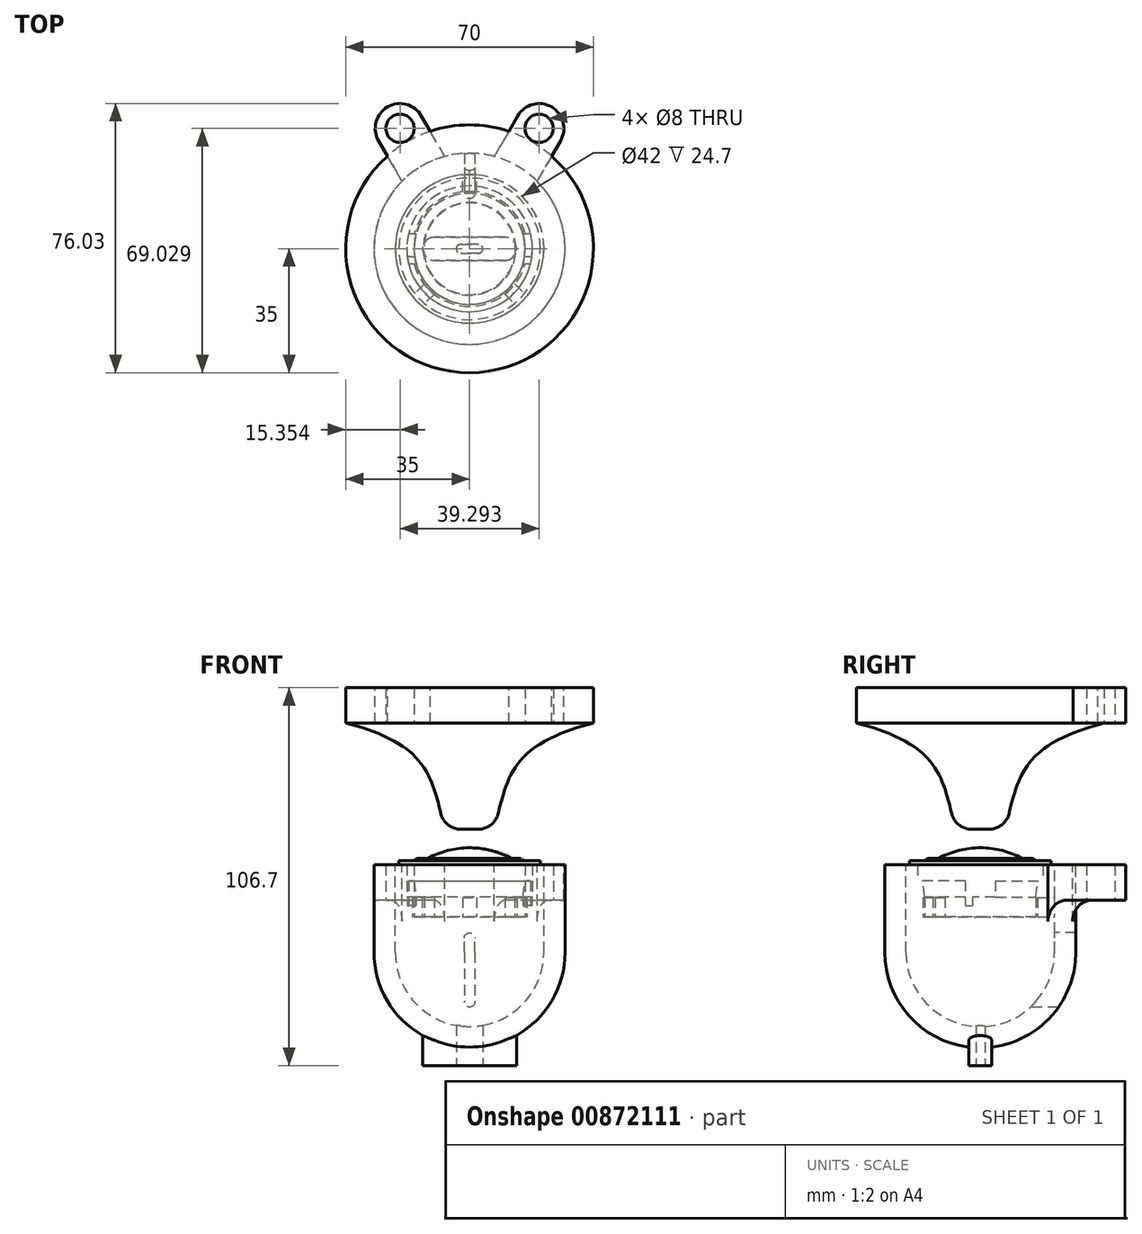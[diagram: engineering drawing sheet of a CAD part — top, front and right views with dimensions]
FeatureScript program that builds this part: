
annotation { "Feature Type Name" : "Feature", "Feature Type Description" : "" }
export const myFeature = defineFeature(function(context is Context, id is Id, definition is map)
    precondition{}
    {
        {
            var Q0;
            Q0=qCreatedBy(makeId("Top.planeOp"),FACE);
            var sketch = newSketch(context, id + "F0", { "sketchPlane" : qUnion([Q0])});
            skCircle(sketch, "E0", {"center": v(0, 0) * mm, "radius": 15.7 * mm});
            skSolve(sketch);
        }
        {
            var Q0;
            Q0 = qSketchRegion(id + "F0", true);
            extrude(context, id + "F1", {"entities" : qUnion([Q0]), "depth" : 5.6 * mm, "offsetDistance" : 25 * mm});
        }
        {
            var Q0;
            Q0=makeQuery(id+"F1.opExtrude","CAP_FACE",FACE,{"disambiguationData":[OSD([sQuery(id+"F0.wireOp",EDGE,"E0")])],"isStart":false});
            cPlane(context, id + "F2", {"entities" : qUnion([Q0]), "cplaneType" : CPlaneType.OFFSET, "offset" : 4.6 * mm, "width" : 150 * mm, "height" : 150 * mm});
        }
        {
            var Q0;
            Q0=makeQuery(id+"F1.opExtrude","CAP_FACE",FACE,{"disambiguationData":[OSD([sQuery(id+"F0.wireOp",EDGE,"E0")])],"isStart":false});
            var sketch = newSketch(context, id + "F3", { "sketchPlane" : qUnion([Q0])});
            skCircle(sketch, "E1.0", {"center": v(0, 0) * mm, "radius": 15.7 * mm});
            skSolve(sketch);
        }
        {
            var Q0;
            Q0=qCreatedBy(id+"F2.planeOp",FACE);
            var sketch = newSketch(context, id + "F4", { "sketchPlane" : qUnion([Q0])});
            skCircle(sketch, "E2", {"center": v(0, 0) * mm, "radius": 16.25 * mm});
            skSolve(sketch);
        }
        {
            var Q1;
            Q1=makeQuery(id+"F3.imprint","IMPRINT",FACE,{"disambiguationData":[TD([[makeQuery(id+"F3.imprint","IMPRINT",EDGE,{"derivedFrom":sQuery(id+"F3.wireOp",EDGE,"E1.0")}),1.0]])]});
            var Q2;
            Q2=makeQuery(id+"F4.imprint","IMPRINT",FACE,{"disambiguationData":[TD([[makeQuery(id+"F4.imprint","IMPRINT",EDGE,{"derivedFrom":sQuery(id+"F4.wireOp",EDGE,"E2")}),1.0]])]});
            loft(context, id + "F5", {"operationType" : NewBodyOperationType.ADD, "sheetProfilesArray" : [{ "sheetProfileEntities" : qUnion([Q1]) }, { "sheetProfileEntities" : qUnion([Q2]) }]});
        }
        {
            var Q0;
            Q0=makeQuery(id+"F5.opLoft","CAP_FACE",FACE,{"disambiguationData":[OSD([makeQuery(id+"F4.imprint","IMPRINT",FACE,{"disambiguationData":[TD([[makeQuery(id+"F4.imprint","IMPRINT",EDGE,{"derivedFrom":sQuery(id+"F4.wireOp",EDGE,"E2")}),1.0]])]})])],"isStart":true});
            var sketch = newSketch(context, id + "F6", { "sketchPlane" : qUnion([Q0])});
            skCircle(sketch, "E3", {"center": v(0, 0) * mm, "radius": 17.75 * mm});
            skSolve(sketch);
        }
        {
            var Q0;
            Q0 = qSketchRegion(id + "F6", true);
            extrude(context, id + "F7", {"entities" : qUnion([Q0]), "operationType" : NewBodyOperationType.ADD, "depth" : 4.5 * mm, "offsetDistance" : 25 * mm});
        }
        {
            var Q0;
            Q0=makeQuery(id+"F7.opExtrude","CAP_FACE",FACE,{"disambiguationData":[OSD([sQuery(id+"F6.wireOp",EDGE,"E3")])],"isStart":false});
            var sketch = newSketch(context, id + "F8", { "sketchPlane" : qUnion([Q0])});
            skCircle(sketch, "E4", {"center": v(0, 0) * mm, "radius": 20 * mm});
            skSolve(sketch);
        }
        {
            var Q0;
            Q0 = qSketchRegion(id + "F8", true);
            extrude(context, id + "F9", {"entities" : qUnion([Q0]), "operationType" : NewBodyOperationType.ADD, "depth" : 1.2 * mm, "offsetDistance" : 25 * mm});
        }
        {
            var Q0;
            Q0=qCreatedBy(makeId("Front.planeOp"),FACE);
            var sketch = newSketch(context, id + "F10", { "sketchPlane" : qUnion([Q0])});
            skCircle(sketch, "E5", {"center": v(-14.38, 14.9) * mm, "radius": 1.62 * mm});
            skLineSegment(sketch, "E6", {"start": v(-12.75, 17.4) * mm, "end": v(-12.75, 14.93) * mm, "construction": true});
            skLineSegment(sketch, "E7", {"start": v(-16, 17.73) * mm, "end": v(-16, 14.12) * mm, "construction": true});
            skSolve(sketch);
        }
        {
            var Q0;
            Q0 = qSketchRegion(id + "F10", true);
            var Q1;
            Q1=makeQuery(id+"F1.opExtrude","SWEPT_FACE",FACE,{"disambiguationData":[OSD([sQuery(id+"F0.wireOp",EDGE,"E0")])]});
            revolve(context, id + "F11", {"operationType" : NewBodyOperationType.ADD, "surfaceOperationType" : NewSurfaceOperationType.NEW, "entities" : qUnion([Q0]), "axis" : qUnion([Q1]), "revolveType" : RevolveType.FULL});
        }
        {
            var Q0;
            Q0=qCreatedBy(makeId("Front.planeOp"),FACE);
            var sketch = newSketch(context, id + "F12", { "sketchPlane" : qUnion([Q0])});
            skArc(sketch, "E8", {"start": v(0, 19.5) * mm, "mid": v(-8.14, 18.14) * mm, "end": v(-15.4, 14.2) * mm});
            skLineSegment(sketch, "E9", {"start": v(-9, 19.5) * mm, "end": v(9, 19.5) * mm, "construction": true});
            skLineSegment(sketch, "E10", {"start": v(-15.4, 14.2) * mm, "end": v(0, 14.2) * mm});
            skLineSegment(sketch, "E11", {"start": v(0, 21.06) * mm, "end": v(0, 12) * mm});
            skSolve(sketch);
        }
        {
            var Q0;
            Q0 = qSketchRegion(id + "F12", true);
            var Q1;
            Q1=sQuery(id+"F12.wireOp",EDGE,"E11");
            revolve(context, id + "F13", {"operationType" : NewBodyOperationType.ADD, "surfaceOperationType" : NewSurfaceOperationType.NEW, "entities" : qUnion([Q0]), "axis" : qUnion([Q1]), "revolveType" : RevolveType.FULL});
        }
        {
            var Q0;
            Q0=qCreatedBy(makeId("Right.planeOp"),FACE);
            var sketch = newSketch(context, id + "F14", { "sketchPlane" : qUnion([Q0])});
            skLineSegment(sketch, "E12.bottom", {"start": v(-4.25, 10.2) * mm, "end": v(4.25, 10.2) * mm});
            skLineSegment(sketch, "E12.top", {"start": v(-4.25, 5.6) * mm, "end": v(4.25, 5.6) * mm});
            skLineSegment(sketch, "E12.left", {"start": v(-4.25, 10.2) * mm, "end": v(-4.25, 5.6) * mm});
            skLineSegment(sketch, "E12.right", {"start": v(4.25, 10.2) * mm, "end": v(4.25, 5.6) * mm});
            skPoint(sketch, "E13", {"position": v(0, 5.6) * mm});
            skLineSegment(sketch, "E14.bottom", {"start": v(-4.25, 5.6) * mm, "end": v(-2.25, 5.6) * mm});
            skLineSegment(sketch, "E14.top", {"start": v(-4.25, 3.1) * mm, "end": v(-2.25, 3.1) * mm});
            skLineSegment(sketch, "E14.left", {"start": v(-4.25, 5.6) * mm, "end": v(-4.25, 3.1) * mm});
            skLineSegment(sketch, "E14.right", {"start": v(-2.25, 5.6) * mm, "end": v(-2.25, 3.1) * mm});
            skSolve(sketch);
        }
        {
            var Q0;
            Q0 = qSketchRegion(id + "F14", true);
            var Q1;
            Q1=makeQuery(id+"F7.opExtrude","SWEPT_FACE",FACE,{"disambiguationData":[OSD([sQuery(id+"F6.wireOp",EDGE,"E3")])]});
            var Q2;
            Q2=makeQuery(id+"F7.opExtrude","SWEPT_FACE",FACE,{"disambiguationData":[OSD([sQuery(id+"F6.wireOp",EDGE,"E3")])]});
            extrude(context, id + "F15", {"entities" : qUnion([Q0]), "operationType" : NewBodyOperationType.ADD, "endBound" : BoundingType.UP_TO_SURFACE, "depth" : 25 * mm, "endBoundEntityFace" : qUnion([Q1]), "offsetDistance" : 25 * mm, "hasSecondDirection" : true, "secondDirectionBound" : BoundingType.UP_TO_SURFACE, "secondDirectionOppositeDirection" : true, "secondDirectionDepth" : 25 * mm, "secondDirectionBoundEntityFace" : qUnion([Q2])});
        }
        {
            var Q0;
            Q0=qCreatedBy(makeId("Front.planeOp"),FACE);
            var sketch = newSketch(context, id + "F16", { "sketchPlane" : qUnion([Q0])});
            skLineSegment(sketch, "E15", {"start": v(-21, 14.7) * mm, "end": v(-21, -10) * mm});
            skArc(sketch, "E16", {"start": v(-21, -10) * mm, "mid": v(-14.85, -24.85) * mm, "end": v(0, -31) * mm});
            skLineSegment(sketch, "E17", {"start": v(0, 25.8) * mm, "end": v(0, -46.07) * mm, "construction": true});
            skArc(sketch, "E18.0", {"start": v(-27, -10) * mm, "mid": v(-19.1, -29.1) * mm, "end": v(0, -37) * mm});
            skLineSegment(sketch, "E18.1", {"start": v(-27, 14.7) * mm, "end": v(-27, -10) * mm});
            skLineSegment(sketch, "E19", {"start": v(-27, 14.7) * mm, "end": v(-21, 14.7) * mm});
            skLineSegment(sketch, "E20", {"start": v(0, -31) * mm, "end": v(0, -37) * mm});
            skSolve(sketch);
        }
        {
            var Q0;
            Q0 = qSketchRegion(id + "F16", true);
            var Q1;
            Q1=sQuery(id+"F16.wireOp",EDGE,"E17");
            revolve(context, id + "F17", {"surfaceOperationType" : NewSurfaceOperationType.NEW, "entities" : qUnion([Q0]), "axis" : qUnion([Q1]), "revolveType" : RevolveType.FULL});
        }
        {
            var Q0;
            Q0=makeQuery(id+"F1.opExtrude","CAP_FACE",FACE,{"disambiguationData":[OSD([sQuery(id+"F0.wireOp",EDGE,"E0")])],"isStart":true});
            var sketch = newSketch(context, id + "F18", { "sketchPlane" : qUnion([Q0])});
            skLineSegment(sketch, "E21", {"start": v(0, 0) * mm, "end": v(0, -21) * mm, "construction": true});
            skLineSegment(sketch, "E22", {"start": v(0, 0) * mm, "end": v(14.85, 14.85) * mm, "construction": true});
            skLineSegment(sketch, "E23", {"start": v(0, 0) * mm, "end": v(-14.85, 14.85) * mm, "construction": true});
            skArc(sketch, "E24.0", {"start": v(-9.95, 12.78) * mm, "mid": v(-11.46, 11.46) * mm, "end": v(-12.78, 9.95) * mm});
            skArc(sketch, "E25", {"start": v(-13.37, 16.2) * mm, "mid": v(-14.85, 14.85) * mm, "end": v(-16.2, 13.37) * mm});
            skLineSegment(sketch, "E26.0", {"start": v(-9.95, 12.78) * mm, "end": v(-13.37, 16.2) * mm});
            skLineSegment(sketch, "E26.1", {"start": v(9.95, 12.78) * mm, "end": v(13.37, 16.2) * mm});
            skLineSegment(sketch, "E27.0", {"start": v(-12.78, 9.95) * mm, "end": v(-16.2, 13.37) * mm});
            skLineSegment(sketch, "E27.1", {"start": v(12.78, 9.95) * mm, "end": v(16.2, 13.37) * mm});
            skLineSegment(sketch, "E28.0", {"start": v(-2, -16.08) * mm, "end": v(-2, -20.9) * mm});
            skLineSegment(sketch, "E29.0", {"start": v(2, -16.08) * mm, "end": v(2, -20.9) * mm});
            skArc(sketch, "E30.trimOffspring", {"start": v(-2, -20.9) * mm, "mid": v(0, -21) * mm, "end": v(2, -20.9) * mm});
            skArc(sketch, "E31.trimOffspring", {"start": v(-2, -16.08) * mm, "mid": v(0, -16.2) * mm, "end": v(2, -16.08) * mm});
            skArc(sketch, "E32.trimOffspring", {"start": v(12.78, 9.95) * mm, "mid": v(11.46, 11.46) * mm, "end": v(9.95, 12.78) * mm});
            skArc(sketch, "E33.trimOffspring", {"start": v(16.2, 13.37) * mm, "mid": v(14.85, 14.85) * mm, "end": v(13.37, 16.2) * mm});
            skSolve(sketch);
        }
        {
            var Q0;
            Q0 = qSketchRegion(id + "F18", true);
            var Q1;
            {var subQ1=sQuery(id+"F14.wireOp",EDGE,"E14.left");var subQ4=sQuery(id+"F14.wireOp",EDGE,"E12.left");var subQ7=sQuery(id+"F6.wireOp",EDGE,"E3");Q1=makeQuery(id+"F15.boolean.opBoolean","SPLIT",FACE,{"disambiguationData":[TD([makeQuery(id+"F15.opExtrude","SWEPT_FACE",FACE,{"disambiguationData":[OSD([subQ4,subQ1])]})])],"derivedFrom":makeQuery(id+"F7.opExtrude","CAP_FACE",FACE,{"disambiguationData":[OSD([subQ7])],"isStart":true})});}
            extrude(context, id + "F19", {"entities" : qUnion([Q0]), "operationType" : NewBodyOperationType.ADD, "oppositeDirection" : true, "depth" : 5.5 * mm, "endBoundEntityFace" : qUnion([Q1]), "offsetDistance" : 25 * mm});
        }
        {
            var Q0;
            Q0=qCreatedBy(makeId("Front.planeOp"),FACE);
            var sketch = newSketch(context, id + "F20", { "sketchPlane" : qUnion([Q0])});
            skLineSegment(sketch, "E34", {"start": v(0, -6) * mm, "end": v(0, -24) * mm});
            skArc(sketch, "E35.0.startCap", {"start": v(-1.5, -6) * mm, "mid": v(0, -4.5) * mm, "end": v(1.5, -6) * mm});
            skArc(sketch, "E35.0.endCap", {"start": v(1.5, -24) * mm, "mid": v(0, -25.5) * mm, "end": v(-1.5, -24) * mm});
            skLineSegment(sketch, "E35.0.left", {"start": v(1.5, -6) * mm, "end": v(1.5, -24) * mm});
            skLineSegment(sketch, "E35.0.right", {"start": v(-1.5, -6) * mm, "end": v(-1.5, -24) * mm});
            skSolve(sketch);
        }
        {
            var Q0;
            Q0 = qSketchRegion(id + "F20", true);
            extrude(context, id + "F21", {"entities" : qUnion([Q0]), "operationType" : NewBodyOperationType.REMOVE, "endBound" : BoundingType.THROUGH_ALL, "oppositeDirection" : true, "depth" : 25 * mm, "offsetDistance" : 25 * mm});
        }
        {
            var Q0;
            Q0=sQuery(id+"F16.wireOp",EDGE,"E17");
            var Q1;
            Q1=sQuery(id+"F16.wireOp",VERTEX,"E18.0.end");
            cPlane(context, id + "F22", {"entities" : qUnion([Q0, Q1]), "cplaneType" : CPlaneType.LINE_POINT, "offset" : 25 * mm, "width" : 150 * mm, "height" : 150 * mm});
        }
        {
            var Q0;
            Q0=qCreatedBy(id+"F22.planeOp",FACE);
            var sketch = newSketch(context, id + "F23", { "sketchPlane" : qUnion([Q0])});
            skLineSegment(sketch, "E36", {"start": v(-10, 0) * mm, "end": v(10, 0) * mm});
            skArc(sketch, "E37.0.startCap", {"start": v(-10, -3.25) * mm, "mid": v(-13.25, 0) * mm, "end": v(-10, 3.25) * mm});
            skArc(sketch, "E37.0.endCap", {"start": v(10, 3.25) * mm, "mid": v(13.25, 0) * mm, "end": v(10, -3.25) * mm});
            skLineSegment(sketch, "E37.0.left", {"start": v(-10, 3.25) * mm, "end": v(10, 3.25) * mm});
            skLineSegment(sketch, "E37.0.right", {"start": v(-10, -3.25) * mm, "end": v(10, -3.25) * mm});
            skArc(sketch, "E38.0.startCap", {"start": v(-10, -3.25) * mm, "mid": v(-13.25, 0) * mm, "end": v(-10, 3.25) * mm, "construction": true});
            skArc(sketch, "E38.0.endCap", {"start": v(10, 3.25) * mm, "mid": v(13.25, 0) * mm, "end": v(10, -3.25) * mm, "construction": true});
            skLineSegment(sketch, "E38.0.left", {"start": v(-10, 3.25) * mm, "end": v(10, 3.25) * mm, "construction": true});
            skLineSegment(sketch, "E38.0.right", {"start": v(-10, -3.25) * mm, "end": v(10, -3.25) * mm, "construction": true});
            skSolve(sketch);
        }
        {
            var Q0;
            Q0 = qSketchRegion(id + "F23", true);
            extrude(context, id + "F24", {"entities" : qUnion([Q0]), "operationType" : NewBodyOperationType.ADD, "endBound" : BoundingType.UP_TO_NEXT, "oppositeDirection" : true, "depth" : 25 * mm, "offsetDistance" : 25 * mm, "hasSecondDirection" : true, "secondDirectionOppositeDirection" : false, "secondDirectionDepth" : 5 * mm});
        }
        {
            var Q0;
            Q0=makeQuery(id+"F17.opRevolve","SWEPT_FACE",FACE,{"disambiguationData":[OSD([sQuery(id+"F16.wireOp",EDGE,"E19")])]});
            cPlane(context, id + "F25", {"entities" : qUnion([Q0]), "cplaneType" : CPlaneType.OFFSET, "offset" : 10 * mm, "width" : 150 * mm, "height" : 150 * mm});
        }
        {
            var Q0;
            Q0=qCreatedBy(id+"F25.planeOp",FACE);
            var sketch = newSketch(context, id + "F26", { "sketchPlane" : qUnion([Q0])});
            skCircle(sketch, "E39", {"center": v(0, 0) * mm, "radius": 7.5 * mm});
            skPoint(sketch, "E40", {"position": v(-7.5, 0) * mm});
            skSolve(sketch);
        }
        {
            var Q0;
            Q0=qCreatedBy(id+"F25.planeOp",FACE);
            cPlane(context, id + "F27", {"entities" : qUnion([Q0]), "cplaneType" : CPlaneType.OFFSET, "offset" : 30 * mm, "width" : 150 * mm, "height" : 150 * mm});
        }
        {
            var Q0;
            Q0=qCreatedBy(id+"F27.planeOp",FACE);
            var sketch = newSketch(context, id + "F28", { "sketchPlane" : qUnion([Q0])});
            skCircle(sketch, "E41", {"center": v(0, 0) * mm, "radius": 35 * mm});
            skPoint(sketch, "E42", {"position": v(-35, 0) * mm});
            skSolve(sketch);
        }
        {
            var Q0;
            Q0=qCreatedBy(makeId("Front.planeOp"),FACE);
            var sketch = newSketch(context, id + "F29", { "sketchPlane" : qUnion([Q0])});
            skPoint(sketch, "E43", {"position": v(-12.77, 42) * mm});
            skPoint(sketch, "E44", {"position": v(-9, 32.7) * mm});
            skFitSpline(sketch, "E45", {"points": [v(-7.5, 24.7) * mm, v(-9, 32.7) * mm, v(-12.77, 42) * mm, v(-35, 54.7) * mm], "startDerivative": vector(-5.93, 52) * mm, "endDerivative": vector(-83.34, 20.66) * mm});
            skLineSegment(sketch, "E46", {"start": v(0, 54.7) * mm, "end": v(0, 24.7) * mm});
            skLineSegment(sketch, "E47", {"start": v(-35, 54.7) * mm, "end": v(0, 54.7) * mm});
            skLineSegment(sketch, "E48", {"start": v(0, 24.7) * mm, "end": v(-7.5, 24.7) * mm});
            skSolve(sketch);
        }
        {
            var Q0;
            Q0=makeQuery(id+"F29.imprint","IMPRINT",FACE,{"disambiguationData":[TD([[makeQuery(id+"F29.imprint","IMPRINT",EDGE,{"derivedFrom":sQuery(id+"F29.wireOp",EDGE,"E45")}),-1.0]])]});
            var Q1;
            Q1=sQuery(id+"F29.wireOp",EDGE,"E46");
            revolve(context, id + "F30", {"surfaceOperationType" : NewSurfaceOperationType.NEW, "entities" : qUnion([Q0]), "axis" : qUnion([Q1]), "revolveType" : RevolveType.FULL});
        }
        {
            var Q0;
            Q0=makeQuery(id+"F30.opRevolve","SWEPT_FACE",FACE,{"disambiguationData":[OSD([sQuery(id+"F29.wireOp",EDGE,"E47")])]});
            var sketch = newSketch(context, id + "F31", { "sketchPlane" : qUnion([Q0])});
            skCircle(sketch, "E49.0", {"center": v(0, 0) * mm, "radius": 35 * mm});
            skSolve(sketch);
        }
        {
            var Q0;
            Q0 = qSketchRegion(id + "F31", true);
            extrude(context, id + "F32", {"entities" : qUnion([Q0]), "operationType" : NewBodyOperationType.ADD, "depth" : 10 * mm, "offsetDistance" : 25 * mm});
        }
        {
            var Q0;
            Q0=makeQuery(id+"F24.opExtrude","CAP_FACE",FACE,{"disambiguationData":[OSD([sQuery(id+"F23.wireOp",EDGE,"E37.0.startCap"),sQuery(id+"F23.wireOp",EDGE,"E37.0.endCap"),sQuery(id+"F23.wireOp",EDGE,"E37.0.left"),sQuery(id+"F23.wireOp",EDGE,"E37.0.right")])],"isStart":true});
            var sketch = newSketch(context, id + "F33", { "sketchPlane" : qUnion([Q0])});
            skLineSegment(sketch, "E50", {"start": v(-2.5, 0) * mm, "end": v(2.5, 0) * mm});
            skArc(sketch, "E51.0.startCap", {"start": v(-2.5, -1.25) * mm, "mid": v(-3.75, 0) * mm, "end": v(-2.5, 1.25) * mm});
            skArc(sketch, "E51.0.endCap", {"start": v(2.5, 1.25) * mm, "mid": v(3.75, 0) * mm, "end": v(2.5, -1.25) * mm});
            skLineSegment(sketch, "E51.0.left", {"start": v(-2.5, 1.25) * mm, "end": v(2.5, 1.25) * mm});
            skLineSegment(sketch, "E51.0.right", {"start": v(-2.5, -1.25) * mm, "end": v(2.5, -1.25) * mm});
            skSolve(sketch);
        }
        {
            var Q0;
            Q0 = qSketchRegion(id + "F33", true);
            extrude(context, id + "F34", {"entities" : qUnion([Q0]), "operationType" : NewBodyOperationType.REMOVE, "endBound" : BoundingType.UP_TO_NEXT, "oppositeDirection" : true, "depth" : 25 * mm, "offsetDistance" : 25 * mm});
        }
        {
            var Q0;
            Q0=makeQuery(id+"F17.opRevolve","SWEPT_FACE",FACE,{"disambiguationData":[OSD([sQuery(id+"F16.wireOp",EDGE,"E19")])]});
            var sketch = newSketch(context, id + "F35", { "sketchPlane" : qUnion([Q0])});
            skLineSegment(sketch, "E52.bottom", {"start": v(-5, -26.53) * mm, "end": v(5, -26.53) * mm});
            skLineSegment(sketch, "E52.top", {"start": v(-5, -33.53) * mm, "end": v(5, -33.53) * mm, "construction": true});
            skLineSegment(sketch, "E52.left", {"start": v(-5, -26.53) * mm, "end": v(-5, -33.53) * mm});
            skLineSegment(sketch, "E52.right", {"start": v(5, -26.53) * mm, "end": v(5, -33.53) * mm});
            skLineSegment(sketch, "E53", {"start": v(0, -33.53) * mm, "end": v(0, 0) * mm, "construction": true});
            skArc(sketch, "E54", {"start": v(-5, -33.53) * mm, "mid": v(0, -38.53) * mm, "end": v(5, -33.53) * mm});
            skSolve(sketch);
        }
        {
            var Q0;
            Q0=makeQuery(id+"F32.opExtrude","CAP_FACE",FACE,{"disambiguationData":[OSD([sQuery(id+"F31.wireOp",EDGE,"E49.0")])],"isStart":false});
            var sketch = newSketch(context, id + "F36", { "sketchPlane" : qUnion([Q0])});
            skLineSegment(sketch, "E55.bottom", {"start": v(-5, -34.64) * mm, "end": v(5, -34.64) * mm});
            skLineSegment(sketch, "E55.top", {"start": v(-5, -39.64) * mm, "end": v(5, -39.64) * mm, "construction": true});
            skLineSegment(sketch, "E55.left", {"start": v(-5, -34.64) * mm, "end": v(-5, -39.64) * mm});
            skLineSegment(sketch, "E55.right", {"start": v(5, -34.64) * mm, "end": v(5, -39.64) * mm});
            skArc(sketch, "E56", {"start": v(-5, -39.64) * mm, "mid": v(0, -44.64) * mm, "end": v(5, -39.64) * mm});
            skLineSegment(sketch, "E57", {"start": v(0, 0) * mm, "end": v(-23.15, 40.1) * mm, "construction": true});
            skLineSegment(sketch, "E58", {"start": v(23.15, 40.1) * mm, "end": v(0, 0) * mm, "construction": true});
            skLineSegment(sketch, "E59", {"start": v(0, 0) * mm, "end": v(0, 42.3) * mm, "construction": true});
            skLineSegment(sketch, "E60.0", {"start": v(-11.08, 33.2) * mm, "end": v(-13.58, 37.53) * mm});
            skLineSegment(sketch, "E61.0", {"start": v(-23.2, 26.2) * mm, "end": v(-25.7, 30.53) * mm});
            skLineSegment(sketch, "E61.1", {"start": v(25.7, 30.53) * mm, "end": v(23.2, 26.2) * mm});
            skLineSegment(sketch, "E62", {"start": v(-23.2, 26.2) * mm, "end": v(-11.08, 33.2) * mm});
            skLineSegment(sketch, "E63", {"start": v(11.08, 33.2) * mm, "end": v(23.2, 26.2) * mm});
            skArc(sketch, "E64", {"start": v(-13.58, 37.53) * mm, "mid": v(-23.15, 40.1) * mm, "end": v(-25.7, 30.53) * mm});
            skArc(sketch, "E65", {"start": v(25.7, 30.53) * mm, "mid": v(23.15, 40.1) * mm, "end": v(13.58, 37.53) * mm});
            skPoint(sketch, "E66.orphan", {"position": v(-27.38, 47.43) * mm});
            skLineSegment(sketch, "E67.trimOffspring", {"start": v(13.58, 37.53) * mm, "end": v(11.08, 33.2) * mm});
            skPoint(sketch, "E68.end.orphan", {"position": v(27.38, 47.43) * mm});
            skLineSegment(sketch, "E69", {"start": v(13.58, 37.53) * mm, "end": v(25.7, 30.53) * mm, "construction": true});
            skSolve(sketch);
        }
        {
            var Q0;
            {var subQ0=sQuery(id+"F36.wireOp",EDGE,"E60.0");Q0=makeQuery(id+"F36.imprint","IMPRINT",FACE,{"disambiguationData":[TD([[makeQuery(id+"F36.imprint","IMPRINT",EDGE,{"derivedFrom":subQ0}),1.0]])]});}
            var Q1;
            {var subQ0=sQuery(id+"F36.wireOp",EDGE,"E61.1");Q1=makeQuery(id+"F36.imprint","IMPRINT",FACE,{"disambiguationData":[TD([[makeQuery(id+"F36.imprint","IMPRINT",EDGE,{"derivedFrom":subQ0}),-1.0]])]});}
            var Q2;
            Q2=makeQuery(id+"F30.opRevolve","SWEPT_FACE",FACE,{"disambiguationData":[OSD([sQuery(id+"F29.wireOp",EDGE,"E45")])]});
            extrude(context, id + "F37", {"entities" : qUnion([Q0, Q1]), "operationType" : NewBodyOperationType.ADD, "oppositeDirection" : true, "depth" : 10 * mm, "endBoundEntityFace" : qUnion([Q2]), "offsetDistance" : 25 * mm});
        }
        {
            var Q0;
            Q0=makeQuery(id+"F17.opRevolve","SWEPT_FACE",FACE,{"disambiguationData":[OSD([sQuery(id+"F16.wireOp",EDGE,"E19")])]});
            var sketch = newSketch(context, id + "F38", { "sketchPlane" : qUnion([Q0])});
            skLineSegment(sketch, "E70.0", {"start": v(25.7, 30.53) * mm, "end": v(23.2, 26.2) * mm});
            skArc(sketch, "E70.1", {"start": v(25.7, 30.53) * mm, "mid": v(23.15, 40.1) * mm, "end": v(13.58, 37.53) * mm});
            skLineSegment(sketch, "E70.2", {"start": v(13.58, 37.53) * mm, "end": v(11.08, 33.2) * mm});
            skLineSegment(sketch, "E70.3", {"start": v(11.08, 33.2) * mm, "end": v(23.2, 26.2) * mm});
            skLineSegment(sketch, "E71.0", {"start": v(-23.2, 26.2) * mm, "end": v(-25.7, 30.53) * mm});
            skLineSegment(sketch, "E71.1", {"start": v(-11.08, 33.2) * mm, "end": v(-13.58, 37.53) * mm});
            skArc(sketch, "E71.2", {"start": v(-13.58, 37.53) * mm, "mid": v(-23.15, 40.1) * mm, "end": v(-25.7, 30.53) * mm});
            skLineSegment(sketch, "E71.3", {"start": v(-23.2, 26.2) * mm, "end": v(-11.08, 33.2) * mm});
            skLineSegment(sketch, "E72", {"start": v(-23.2, 26.2) * mm, "end": v(-19.1, 19.08) * mm});
            skLineSegment(sketch, "E73", {"start": v(-19.1, 19.08) * mm, "end": v(-6.98, 26.08) * mm});
            skLineSegment(sketch, "E74", {"start": v(-6.98, 26.08) * mm, "end": v(-11.08, 33.2) * mm});
            skLineSegment(sketch, "E75", {"start": v(23.2, 26.2) * mm, "end": v(19.1, 19.08) * mm});
            skLineSegment(sketch, "E76", {"start": v(19.1, 19.08) * mm, "end": v(6.98, 26.08) * mm});
            skLineSegment(sketch, "E77", {"start": v(6.98, 26.08) * mm, "end": v(11.08, 33.2) * mm});
            skSolve(sketch);
        }
        {
            var Q0;
            Q0 = qSketchRegion(id + "F38", true);
            extrude(context, id + "F39", {"entities" : qUnion([Q0]), "operationType" : NewBodyOperationType.ADD, "oppositeDirection" : true, "depth" : 10 * mm, "offsetDistance" : 25 * mm});
        }
        {
            var Q0;
            Q0=makeQuery(id+"F37.opExtrude","SWEPT_EDGE",EDGE,{"disambiguationData":[OSD([sQuery(id+"F31.wireOp",EDGE,"E49.0"),sQuery(id+"F36.wireOp",EDGE,"E55.bottom"),sQuery(id+"F36.wireOp",EDGE,"E55.left")])]});
            var Q1;
            Q1=makeQuery(id+"F37.opExtrude","SWEPT_EDGE",EDGE,{"disambiguationData":[OSD([sQuery(id+"F31.wireOp",EDGE,"E49.0"),sQuery(id+"F36.wireOp",EDGE,"E55.bottom"),sQuery(id+"F36.wireOp",EDGE,"E55.right")])]});
            var Q2;
            Q2=makeQuery(id+"F37.opExtrude","SWEPT_EDGE",EDGE,{"disambiguationData":[OSD([sQuery(id+"F31.wireOp",EDGE,"E49.0"),sQuery(id+"F36.wireOp",EDGE,"E61.0"),sQuery(id+"F36.wireOp",EDGE,"E62")])]});
            var Q3;
            Q3=makeQuery(id+"F37.opExtrude","SWEPT_EDGE",EDGE,{"disambiguationData":[OSD([sQuery(id+"F31.wireOp",EDGE,"E49.0"),sQuery(id+"F36.wireOp",EDGE,"E60.0"),sQuery(id+"F36.wireOp",EDGE,"E62")])]});
            var Q4;
            Q4=makeQuery(id+"F37.opExtrude","SWEPT_EDGE",EDGE,{"disambiguationData":[OSD([sQuery(id+"F31.wireOp",EDGE,"E49.0"),sQuery(id+"F36.wireOp",EDGE,"E61.1"),sQuery(id+"F36.wireOp",EDGE,"E63")])]});
            var Q5;
            Q5=makeQuery(id+"F37.opExtrude","SWEPT_EDGE",EDGE,{"disambiguationData":[OSD([sQuery(id+"F31.wireOp",EDGE,"E49.0"),sQuery(id+"F36.wireOp",EDGE,"E63"),sQuery(id+"F36.wireOp",EDGE,"E67.trimOffspring")])]});
            var Q6;
            Q6=makeQuery(id+"F39.opExtrude","SWEPT_EDGE",EDGE,{"disambiguationData":[OSD([sQuery(id+"F16.wireOp",EDGE,"E18.1"),sQuery(id+"F16.wireOp",EDGE,"E19"),sQuery(id+"F38.wireOp",EDGE,"E75"),sQuery(id+"F38.wireOp",EDGE,"E76")])]});
            var Q7;
            Q7=makeQuery(id+"F39.opExtrude","SWEPT_EDGE",EDGE,{"disambiguationData":[OSD([sQuery(id+"F16.wireOp",EDGE,"E18.1"),sQuery(id+"F16.wireOp",EDGE,"E19"),sQuery(id+"F38.wireOp",EDGE,"E76"),sQuery(id+"F38.wireOp",EDGE,"E77")])]});
            var Q8;
            Q8=makeQuery(id+"F39.opExtrude","SWEPT_EDGE",EDGE,{"disambiguationData":[OSD([sQuery(id+"F16.wireOp",EDGE,"E18.1"),sQuery(id+"F16.wireOp",EDGE,"E19"),sQuery(id+"F38.wireOp",EDGE,"E73"),sQuery(id+"F38.wireOp",EDGE,"E74")])]});
            var Q9;
            Q9=makeQuery(id+"F39.opExtrude","SWEPT_EDGE",EDGE,{"disambiguationData":[OSD([sQuery(id+"F16.wireOp",EDGE,"E18.1"),sQuery(id+"F16.wireOp",EDGE,"E19"),sQuery(id+"F38.wireOp",EDGE,"E72"),sQuery(id+"F38.wireOp",EDGE,"E73")])]});
            var Q10;
            Q10=makeQuery(id+"F39.boolean.opBoolean","INTERSECT",EDGE,{"derivedFrom":[makeQuery(id+"F17.opRevolve","SWEPT_FACE",FACE,{"disambiguationData":[OSD([sQuery(id+"F16.wireOp",EDGE,"E18.1")])]}),makeQuery(id+"F39.opExtrude","CAP_FACE",FACE,{"disambiguationData":[OSD([sQuery(id+"F38.wireOp",EDGE,"E71.0"),sQuery(id+"F38.wireOp",EDGE,"E71.1"),sQuery(id+"F38.wireOp",EDGE,"E71.2"),sQuery(id+"F38.wireOp",EDGE,"E72"),sQuery(id+"F38.wireOp",EDGE,"E73"),sQuery(id+"F38.wireOp",EDGE,"E74")])],"isStart":false})]});
            var Q11;
            Q11=makeQuery(id+"F39.boolean.opBoolean","INTERSECT",EDGE,{"derivedFrom":[makeQuery(id+"F17.opRevolve","SWEPT_FACE",FACE,{"disambiguationData":[OSD([sQuery(id+"F16.wireOp",EDGE,"E18.1")])]}),makeQuery(id+"F39.opExtrude","CAP_FACE",FACE,{"disambiguationData":[OSD([sQuery(id+"F38.wireOp",EDGE,"E70.0"),sQuery(id+"F38.wireOp",EDGE,"E70.1"),sQuery(id+"F38.wireOp",EDGE,"E70.2"),sQuery(id+"F38.wireOp",EDGE,"E75"),sQuery(id+"F38.wireOp",EDGE,"E76"),sQuery(id+"F38.wireOp",EDGE,"E77")])],"isStart":false})]});
            fillet(context, id + "F40", {"entities" : qUnion([Q0, Q1, Q2, Q3, Q4, Q5, Q6, Q7, Q8, Q9, Q10, Q11]), "radius" : 6 * mm, "tangentPropagation" : true, "allowEdgeOverflow" : false});
        }
        {
            var Q0;
            Q0=makeQuery(id+"F37.opExtrude","CAP_FACE",FACE,{"disambiguationData":[OSD([sQuery(id+"F31.wireOp",EDGE,"E49.0"),sQuery(id+"F36.wireOp",EDGE,"E61.1"),sQuery(id+"F36.wireOp",EDGE,"E65"),sQuery(id+"F36.wireOp",EDGE,"E67.trimOffspring")])],"isStart":false});
            var sketch = newSketch(context, id + "F41", { "sketchPlane" : qUnion([Q0])});
            skCircle(sketch, "E78", {"center": v(19.65, -34.03) * mm, "radius": 4 * mm});
            skCircle(sketch, "E79", {"center": v(-19.65, -34.03) * mm, "radius": 4 * mm});
            skSolve(sketch);
        }
        {
            var Q0;
            Q0 = qSketchRegion(id + "F41", true);
            extrude(context, id + "F42", {"entities" : qUnion([Q0]), "operationType" : NewBodyOperationType.REMOVE, "oppositeDirection" : true, "depth" : 6 * mm, "offsetDistance" : 25 * mm});
        }
        {
            var Q0;
            Q0=makeQuery(id+"F39.opExtrude","CAP_FACE",FACE,{"disambiguationData":[OSD([sQuery(id+"F38.wireOp",EDGE,"E70.0"),sQuery(id+"F38.wireOp",EDGE,"E70.1"),sQuery(id+"F38.wireOp",EDGE,"E70.2"),sQuery(id+"F38.wireOp",EDGE,"E75"),sQuery(id+"F38.wireOp",EDGE,"E76"),sQuery(id+"F38.wireOp",EDGE,"E77")])],"isStart":false});
            var sketch = newSketch(context, id + "F43", { "sketchPlane" : qUnion([Q0])});
            skCircle(sketch, "E80.0", {"center": v(19.65, -34.03) * mm, "radius": 4 * mm});
            skCircle(sketch, "E81.0", {"center": v(-19.65, -34.03) * mm, "radius": 4 * mm});
            skSolve(sketch);
        }
        {
            var Q0;
            Q0 = qSketchRegion(id + "F43", true);
            extrude(context, id + "F44", {"entities" : qUnion([Q0]), "operationType" : NewBodyOperationType.REMOVE, "endBound" : BoundingType.THROUGH_ALL, "oppositeDirection" : true, "depth" : 25 * mm, "offsetDistance" : 25 * mm});
        }
        {
            var Q0;
            Q0=makeQuery(id+"F30.opRevolve","SWEPT_EDGE",EDGE,{"disambiguationData":[OSD([sQuery(id+"F29.wireOp",EDGE,"E45"),sQuery(id+"F29.wireOp",EDGE,"E48")])]});
            fillet(context, id + "F45", {"entities" : qUnion([Q0]), "radius" : 6 * mm, "tangentPropagation" : true, "allowEdgeOverflow" : false});
        }
    });
